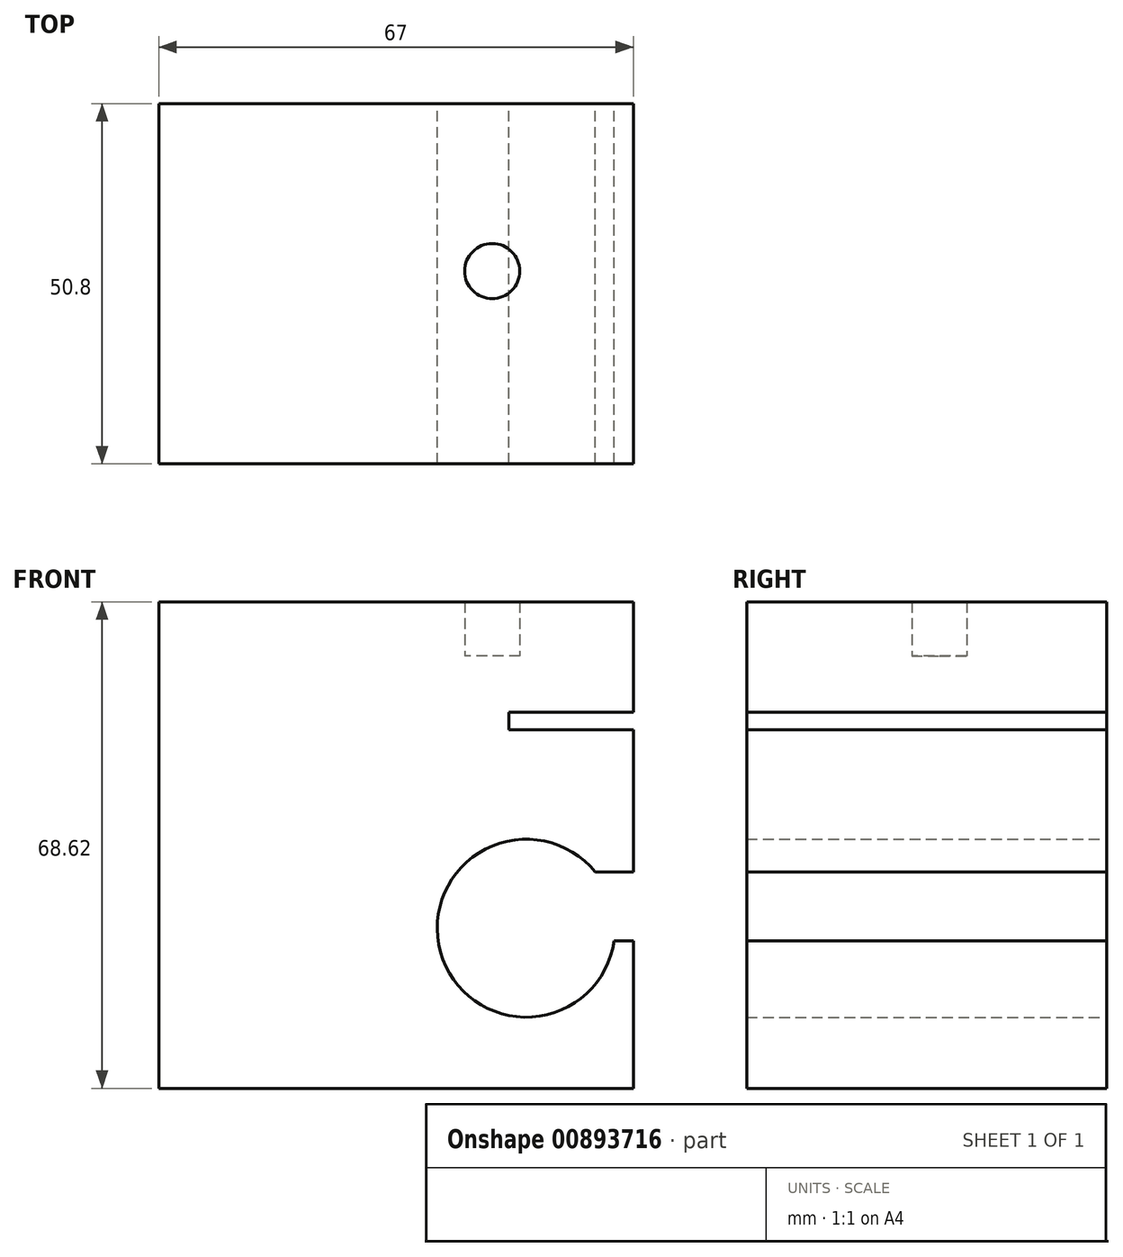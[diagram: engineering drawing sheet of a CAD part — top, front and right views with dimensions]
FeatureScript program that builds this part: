
annotation { "Feature Type Name" : "Feature", "Feature Type Description" : "" }
export const myFeature = defineFeature(function(context is Context, id is Id, definition is map)
    precondition{}
    {
        {
            var Q0;
            Q0=qCreatedBy(makeId("Front.planeOp"),FACE);
            var sketch = newSketch(context, id + "F0", { "sketchPlane" : qUnion([Q0])});
            skLineSegment(sketch, "E0.bottom", {"start": v(-58.9, 2.27) * mm, "end": v(8.1, 2.27) * mm});
            skLineSegment(sketch, "E0.top", {"start": v(-58.9, -58.73) * mm, "end": v(8.1, -58.73) * mm});
            skLineSegment(sketch, "E0.left", {"start": v(-58.9, 2.27) * mm, "end": v(-58.9, -58.73) * mm});
            skLineSegment(sketch, "E0.right", {"start": v(8.1, 2.27) * mm, "end": v(8.1, -58.73) * mm});
            skCircle(sketch, "E1", {"center": v(-7.03, -36.14) * mm, "radius": 12.56 * mm});
            skPoint(sketch, "E2.firstSnap0", {"position": v(8.1, -28.23) * mm});
            skLineSegment(sketch, "E2.bottom", {"start": v(2.64, -28.23) * mm, "end": v(16.33, -28.23) * mm});
            skLineSegment(sketch, "E2.top", {"start": v(2.64, -37.91) * mm, "end": v(16.33, -37.91) * mm});
            skLineSegment(sketch, "E2.left", {"start": v(2.64, -28.23) * mm, "end": v(2.64, -37.91) * mm});
            skLineSegment(sketch, "E2.right", {"start": v(16.33, -28.23) * mm, "end": v(16.33, -37.91) * mm});
            skLineSegment(sketch, "E3.bottom", {"start": v(8.1, -5.64) * mm, "end": v(-9.47, -5.64) * mm});
            skLineSegment(sketch, "E3.top", {"start": v(8.1, -8.15) * mm, "end": v(-9.47, -8.15) * mm});
            skLineSegment(sketch, "E3.left", {"start": v(8.1, -5.64) * mm, "end": v(8.1, -8.15) * mm});
            skLineSegment(sketch, "E3.right", {"start": v(-9.47, -5.64) * mm, "end": v(-9.47, -8.15) * mm});
            skSolve(sketch);
        }
        {
            var Q0;
            Q0=makeQuery(id+"F0.imprint","IMPRINT",FACE,{"disambiguationData":[TD([[makeQuery(id+"F0.imprint","IMPRINT",EDGE,{"derivedFrom":sQuery(id+"F0.wireOp",EDGE,"E0.bottom")}),-1.0]])]});
            extrude(context, id + "F1", {"entities" : qUnion([Q0]), "depth" : 50.8 * mm, "offsetDistance" : 25.4 * mm});
        }
        {
            var Q0;
            Q0=makeQuery(id+"F1.opExtrude","SWEPT_FACE",FACE,{"disambiguationData":[OSD([sQuery(id+"F0.wireOp",EDGE,"E0.bottom")])]});
            var sketch = newSketch(context, id + "F2", { "sketchPlane" : qUnion([Q0])});
            skCircle(sketch, "E4", {"center": v(-11.83, -23.62) * mm, "radius": 3.89 * mm});
            skSolve(sketch);
        }
        {
            var Q0;
            Q0=makeQuery(id+"F2.imprint","IMPRINT",FACE,{"disambiguationData":[TD([[makeQuery(id+"F2.imprint","IMPRINT",EDGE,{"derivedFrom":sQuery(id+"F2.wireOp",EDGE,"E4")}),-1.0]])]});
            extrude(context, id + "F3", {"entities" : qUnion([Q0]), "operationType" : NewBodyOperationType.ADD, "depth" : 7.62 * mm, "offsetDistance" : 25.4 * mm});
        }
    });
